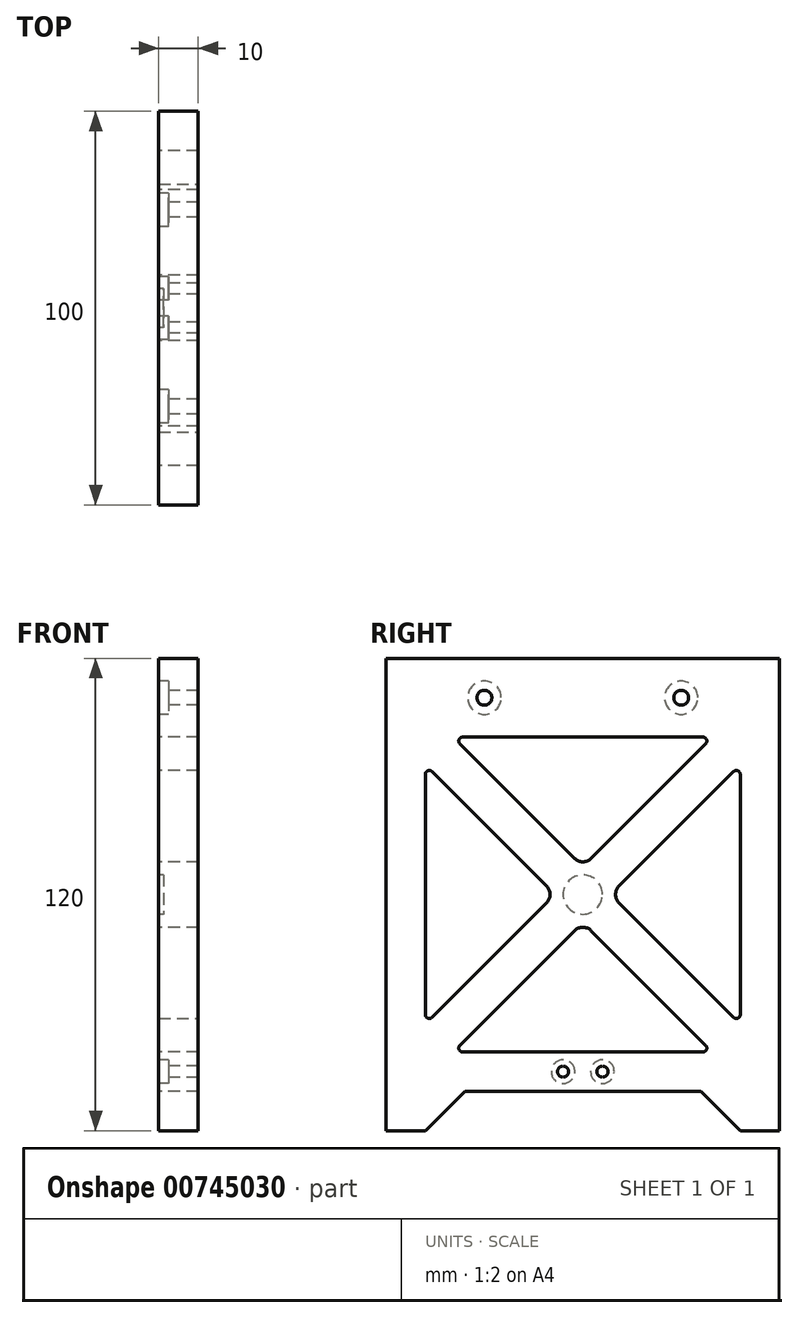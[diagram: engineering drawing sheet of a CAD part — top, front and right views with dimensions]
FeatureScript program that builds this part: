
annotation { "Feature Type Name" : "Feature", "Feature Type Description" : "" }
export const myFeature = defineFeature(function(context is Context, id is Id, definition is map)
    precondition{}
    {
        {
            var Q0;
            Q0=qCreatedBy(makeId("Right.planeOp"),FACE);
            var sketch = newSketch(context, id + "F0", { "sketchPlane" : qUnion([Q0])});
            skLineSegment(sketch, "E0.bottom", {"start": v(50, -60) * mm, "end": v(40.05, -60) * mm});
            skLineSegment(sketch, "E0.top", {"start": v(50, 60) * mm, "end": v(-50, 60) * mm});
            skLineSegment(sketch, "E0.left", {"start": v(50, -60) * mm, "end": v(50, 60) * mm});
            skLineSegment(sketch, "E0.right", {"start": v(-50, -60) * mm, "end": v(-50, 60) * mm});
            skPoint(sketch, "E0.middle", {"position": v(0, 0) * mm});
            skLineSegment(sketch, "E1.bottom", {"start": v(40, -40) * mm, "end": v(-32.93, -40) * mm});
            skLineSegment(sketch, "E1.top", {"start": v(32.93, 40) * mm, "end": v(-32.93, 40) * mm});
            skLineSegment(sketch, "E1.left", {"start": v(40, -40) * mm, "end": v(40, 32.93) * mm});
            skLineSegment(sketch, "E1.right", {"start": v(-40, -32.93) * mm, "end": v(-40, 32.93) * mm});
            skLineSegment(sketch, "E2.trimOffspring", {"start": v(-40, -60) * mm, "end": v(-50, -60) * mm});
            skLineSegment(sketch, "E3", {"start": v(30.05, -50) * mm, "end": v(40.05, -60) * mm});
            skLineSegment(sketch, "E4", {"start": v(30.05, -50) * mm, "end": v(-29.95, -50) * mm});
            skLineSegment(sketch, "E5", {"start": v(-29.95, -50) * mm, "end": v(-40, -60) * mm});
            skLineSegment(sketch, "E6", {"start": v(-40, -32.93) * mm, "end": v(-9.2, -2.12) * mm});
            skLineSegment(sketch, "E7.MirrorCS", {"start": v(-32.93, -40) * mm, "end": v(-2.12, -9.2) * mm});
            skLineSegment(sketch, "E8.trimOffspring", {"start": v(-40, 32.93) * mm, "end": v(-9.2, 2.12) * mm});
            skLineSegment(sketch, "E9.MirrorCS", {"start": v(-32.93, 40) * mm, "end": v(-2.12, 9.2) * mm});
            skLineSegment(sketch, "E10.trimOffspring", {"start": v(9.2, 2.12) * mm, "end": v(40, 32.93) * mm});
            skLineSegment(sketch, "E11.trimOffspring", {"start": v(2.12, -9.2) * mm, "end": v(32.93, -40) * mm});
            skLineSegment(sketch, "E12.trimOffspring", {"start": v(9.2, -2.12) * mm, "end": v(40, -32.93) * mm});
            skLineSegment(sketch, "E13.trimOffspring", {"start": v(2.12, 9.2) * mm, "end": v(32.93, 40) * mm});
            skPoint(sketch, "E14.visualSharp", {"position": v(0, 7.07) * mm});
            skArc(sketch, "E14.filletArc", {"start": v(-2.12, 9.2) * mm, "mid": v(0, 8.31) * mm, "end": v(2.12, 9.2) * mm});
            skPoint(sketch, "E15.visualSharp", {"position": v(0, -7.07) * mm});
            skArc(sketch, "E15.filletArc", {"start": v(2.12, -9.2) * mm, "mid": v(0, -8.31) * mm, "end": v(-2.12, -9.2) * mm});
            skPoint(sketch, "E16.visualSharp", {"position": v(7.07, 0) * mm});
            skArc(sketch, "E16.filletArc", {"start": v(9.2, 2.12) * mm, "mid": v(8.31, 0) * mm, "end": v(9.2, -2.12) * mm});
            skPoint(sketch, "E17.visualSharp", {"position": v(-7.07, 0) * mm});
            skArc(sketch, "E17.filletArc", {"start": v(-9.2, -2.12) * mm, "mid": v(-8.31, 0) * mm, "end": v(-9.2, 2.12) * mm});
            skLineSegment(sketch, "E18", {"start": v(81.83, 50) * mm, "end": v(-92.03, 50) * mm, "construction": true});
            skPoint(sketch, "E19", {"position": v(25, 50) * mm});
            skPoint(sketch, "E20", {"position": v(-25, 50) * mm});
            skSolve(sketch);
        }
        {
            var Q0;
            Q0 = qSketchRegion(id + "F0", true);
            extrude(context, id + "F1", {"entities" : qUnion([Q0]), "depth" : 10 * mm, "offsetDistance" : 25 * mm});
        }
        {
            var Q0;
            Q0=makeQuery(id+"F1.opExtrude","SWEPT_EDGE",EDGE,{"disambiguationData":[OSD([sQuery(id+"F0.wireOp",EDGE,"E1.top"),sQuery(id+"F0.wireOp",EDGE,"E9.MirrorCS")])]});
            var Q1;
            Q1=makeQuery(id+"F1.opExtrude","SWEPT_EDGE",EDGE,{"disambiguationData":[OSD([sQuery(id+"F0.wireOp",EDGE,"E1.top"),sQuery(id+"F0.wireOp",EDGE,"E13.trimOffspring")])]});
            var Q2;
            Q2=makeQuery(id+"F1.opExtrude","SWEPT_EDGE",EDGE,{"disambiguationData":[OSD([sQuery(id+"F0.wireOp",EDGE,"E1.right"),sQuery(id+"F0.wireOp",EDGE,"E8.trimOffspring")])]});
            var Q3;
            Q3=makeQuery(id+"F1.opExtrude","SWEPT_EDGE",EDGE,{"disambiguationData":[OSD([sQuery(id+"F0.wireOp",EDGE,"E1.right"),sQuery(id+"F0.wireOp",EDGE,"E6")])]});
            var Q4;
            Q4=makeQuery(id+"F1.opExtrude","SWEPT_EDGE",EDGE,{"disambiguationData":[OSD([sQuery(id+"F0.wireOp",EDGE,"E1.bottom"),sQuery(id+"F0.wireOp",EDGE,"E7.MirrorCS")])]});
            var Q5;
            Q5=makeQuery(id+"F1.opExtrude","SWEPT_EDGE",EDGE,{"disambiguationData":[OSD([sQuery(id+"F0.wireOp",EDGE,"E1.left"),sQuery(id+"F0.wireOp",EDGE,"E10.trimOffspring")])]});
            var Q6;
            Q6=makeQuery(id+"F1.opExtrude","SWEPT_EDGE",EDGE,{"disambiguationData":[OSD([sQuery(id+"F0.wireOp",EDGE,"E1.left"),sQuery(id+"F0.wireOp",EDGE,"E12.trimOffspring")])]});
            var Q7;
            Q7=makeQuery(id+"F1.opExtrude","SWEPT_EDGE",EDGE,{"disambiguationData":[OSD([sQuery(id+"F0.wireOp",EDGE,"E1.bottom"),sQuery(id+"F0.wireOp",EDGE,"E11.trimOffspring")])]});
            fillet(context, id + "F2", {"entities" : qUnion([Q0, Q1, Q2, Q3, Q4, Q5, Q6, Q7]), "radius" : 1 * mm, "tangentPropagation" : true, "allowEdgeOverflow" : false});
        }
        {
            var Q0;
            Q0=sQuery(id+"F0.wireOp",VERTEX,"E20");
            var Q1;
            Q1=sQuery(id+"F0.wireOp",VERTEX,"E19");
            var Q2;
            Q2=makeQuery(id+"F1.opExtrude","SWEPT_BODY",BODY,{"disambiguationData":[OSD([sQuery(id+"F0.wireOp",EDGE,"E0.bottom"),sQuery(id+"F0.wireOp",EDGE,"E0.top"),sQuery(id+"F0.wireOp",EDGE,"E0.left"),sQuery(id+"F0.wireOp",EDGE,"E0.right"),sQuery(id+"F0.wireOp",EDGE,"E1.bottom"),sQuery(id+"F0.wireOp",EDGE,"E1.top"),sQuery(id+"F0.wireOp",EDGE,"E1.left"),sQuery(id+"F0.wireOp",EDGE,"E1.right"),sQuery(id+"F0.wireOp",EDGE,"E2.trimOffspring"),sQuery(id+"F0.wireOp",EDGE,"E3"),sQuery(id+"F0.wireOp",EDGE,"E4"),sQuery(id+"F0.wireOp",EDGE,"E5"),sQuery(id+"F0.wireOp",EDGE,"E6"),sQuery(id+"F0.wireOp",EDGE,"E7.MirrorCS"),sQuery(id+"F0.wireOp",EDGE,"E8.trimOffspring"),sQuery(id+"F0.wireOp",EDGE,"E9.MirrorCS"),sQuery(id+"F0.wireOp",EDGE,"E10.trimOffspring"),sQuery(id+"F0.wireOp",EDGE,"E11.trimOffspring"),sQuery(id+"F0.wireOp",EDGE,"E12.trimOffspring"),sQuery(id+"F0.wireOp",EDGE,"E13.trimOffspring"),sQuery(id+"F0.wireOp",EDGE,"E14.filletArc"),sQuery(id+"F0.wireOp",EDGE,"E15.filletArc"),sQuery(id+"F0.wireOp",EDGE,"E16.filletArc"),sQuery(id+"F0.wireOp",EDGE,"E17.filletArc")])]});
            hole(context, id + "F3", {"style" : HoleStyle.C_BORE, "endStyle" : HoleEndStyle.THROUGH, "oppositeDirection" : true, "holeDiameter" : 3.8 * mm, "cBoreDiameter" : 8.5 * mm, "cBoreDepth" : 2.5 * mm, "majorDiameter" : 5 * mm, "isTappedThrough" : true, "tappedDepth" : 6 * mm, "tapClearance" : 3, "locations" : qUnion([Q0, Q1]), "scope" : qUnion([Q2])});
        }
        {
            var Q0;
            Q0=makeQuery(id+"F1.opExtrude","CAP_FACE",FACE,{"disambiguationData":[OSD([sQuery(id+"F0.wireOp",EDGE,"E0.bottom"),sQuery(id+"F0.wireOp",EDGE,"E0.top"),sQuery(id+"F0.wireOp",EDGE,"E0.left"),sQuery(id+"F0.wireOp",EDGE,"E0.right"),sQuery(id+"F0.wireOp",EDGE,"E1.bottom"),sQuery(id+"F0.wireOp",EDGE,"E1.top"),sQuery(id+"F0.wireOp",EDGE,"E1.left"),sQuery(id+"F0.wireOp",EDGE,"E1.right"),sQuery(id+"F0.wireOp",EDGE,"E2.trimOffspring"),sQuery(id+"F0.wireOp",EDGE,"E3"),sQuery(id+"F0.wireOp",EDGE,"E4"),sQuery(id+"F0.wireOp",EDGE,"E5"),sQuery(id+"F0.wireOp",EDGE,"E6"),sQuery(id+"F0.wireOp",EDGE,"E7.MirrorCS"),sQuery(id+"F0.wireOp",EDGE,"E8.trimOffspring"),sQuery(id+"F0.wireOp",EDGE,"E9.MirrorCS"),sQuery(id+"F0.wireOp",EDGE,"E10.trimOffspring"),sQuery(id+"F0.wireOp",EDGE,"E11.trimOffspring"),sQuery(id+"F0.wireOp",EDGE,"E12.trimOffspring"),sQuery(id+"F0.wireOp",EDGE,"E13.trimOffspring"),sQuery(id+"F0.wireOp",EDGE,"E14.filletArc"),sQuery(id+"F0.wireOp",EDGE,"E15.filletArc"),sQuery(id+"F0.wireOp",EDGE,"E16.filletArc"),sQuery(id+"F0.wireOp",EDGE,"E17.filletArc")])],"isStart":true});
            var sketch = newSketch(context, id + "F4", { "sketchPlane" : qUnion([Q0])});
            skCircle(sketch, "E21", {"center": v(0, 0) * mm, "radius": 5 * mm});
            skSolve(sketch);
        }
        {
            var Q0;
            Q0=makeQuery(id+"F4.imprint","IMPRINT",FACE,{"disambiguationData":[TD([[makeQuery(id+"F4.imprint","IMPRINT",EDGE,{"derivedFrom":sQuery(id+"F4.wireOp",EDGE,"E21")}),1.0]])]});
            extrude(context, id + "F5", {"entities" : qUnion([Q0]), "operationType" : NewBodyOperationType.REMOVE, "oppositeDirection" : true, "depth" : 1.2 * mm, "offsetDistance" : 25 * mm});
        }
        {
            var Q0;
            Q0=makeQuery(id+"F1.opExtrude","CAP_FACE",FACE,{"disambiguationData":[OSD([sQuery(id+"F0.wireOp",EDGE,"E0.bottom"),sQuery(id+"F0.wireOp",EDGE,"E0.top"),sQuery(id+"F0.wireOp",EDGE,"E0.left"),sQuery(id+"F0.wireOp",EDGE,"E0.right"),sQuery(id+"F0.wireOp",EDGE,"E1.bottom"),sQuery(id+"F0.wireOp",EDGE,"E1.top"),sQuery(id+"F0.wireOp",EDGE,"E1.left"),sQuery(id+"F0.wireOp",EDGE,"E1.right"),sQuery(id+"F0.wireOp",EDGE,"E2.trimOffspring"),sQuery(id+"F0.wireOp",EDGE,"E3"),sQuery(id+"F0.wireOp",EDGE,"E4"),sQuery(id+"F0.wireOp",EDGE,"E5"),sQuery(id+"F0.wireOp",EDGE,"E6"),sQuery(id+"F0.wireOp",EDGE,"E7.MirrorCS"),sQuery(id+"F0.wireOp",EDGE,"E8.trimOffspring"),sQuery(id+"F0.wireOp",EDGE,"E9.MirrorCS"),sQuery(id+"F0.wireOp",EDGE,"E10.trimOffspring"),sQuery(id+"F0.wireOp",EDGE,"E11.trimOffspring"),sQuery(id+"F0.wireOp",EDGE,"E12.trimOffspring"),sQuery(id+"F0.wireOp",EDGE,"E13.trimOffspring"),sQuery(id+"F0.wireOp",EDGE,"E14.filletArc"),sQuery(id+"F0.wireOp",EDGE,"E15.filletArc"),sQuery(id+"F0.wireOp",EDGE,"E16.filletArc"),sQuery(id+"F0.wireOp",EDGE,"E17.filletArc")])],"isStart":true});
            var sketch = newSketch(context, id + "F6", { "sketchPlane" : qUnion([Q0])});
            skPoint(sketch, "E22.0", {"position": v(-50, 60) * mm});
            skPoint(sketch, "E22.1", {"position": v(50, 60) * mm});
            skPoint(sketch, "E22.2", {"position": v(-50, -60) * mm});
            skPoint(sketch, "E22.3", {"position": v(50, -60) * mm});
            skArc(sketch, "E23", {"start": v(-40.05, -60) * mm, "mid": v(-57.03, -67.03) * mm, "end": v(-50, -50.05) * mm});
            skArc(sketch, "E24", {"start": v(40, -60) * mm, "mid": v(57.07, -67.07) * mm, "end": v(50, -50) * mm});
            skArc(sketch, "E25", {"start": v(40, 60) * mm, "mid": v(57.07, 67.07) * mm, "end": v(50, 50) * mm});
            skArc(sketch, "E26", {"start": v(-50, 50) * mm, "mid": v(-57.07, 67.07) * mm, "end": v(-40, 60) * mm});
            skSolve(sketch);
        }
        {
            var Q0;
            {var subQ0=sQuery(id+"F0.wireOp",EDGE,"E0.left");var subQ1=sQuery(id+"F0.wireOp",EDGE,"E0.top");var subQ2=sQuery(id+"F0.wireOp",EDGE,"E0.right");var subQ3=sQuery(id+"F0.wireOp",EDGE,"E2.trimOffspring");var subQ4=sQuery(id+"F0.wireOp",EDGE,"E0.bottom");Q0=makeQuery(id+"FwKSpRcwW1PzX61_1.boolean.opBoolean","MERGE",FACE,{"derivedFrom":[makeQuery(id+"F1.opExtrude","CAP_FACE",FACE,{"disambiguationData":[OSD([subQ4,subQ1,subQ0,subQ2,sQuery(id+"F0.wireOp",EDGE,"E1.bottom"),sQuery(id+"F0.wireOp",EDGE,"E1.top"),sQuery(id+"F0.wireOp",EDGE,"E1.left"),sQuery(id+"F0.wireOp",EDGE,"E1.right"),subQ3,sQuery(id+"F0.wireOp",EDGE,"E3"),sQuery(id+"F0.wireOp",EDGE,"E4"),sQuery(id+"F0.wireOp",EDGE,"E5"),sQuery(id+"F0.wireOp",EDGE,"E6"),sQuery(id+"F0.wireOp",EDGE,"E7.MirrorCS"),sQuery(id+"F0.wireOp",EDGE,"E8.trimOffspring"),sQuery(id+"F0.wireOp",EDGE,"E9.MirrorCS"),sQuery(id+"F0.wireOp",EDGE,"E10.trimOffspring"),sQuery(id+"F0.wireOp",EDGE,"E11.trimOffspring"),sQuery(id+"F0.wireOp",EDGE,"E12.trimOffspring"),sQuery(id+"F0.wireOp",EDGE,"E13.trimOffspring"),sQuery(id+"F0.wireOp",EDGE,"E14.filletArc"),sQuery(id+"F0.wireOp",EDGE,"E15.filletArc"),sQuery(id+"F0.wireOp",EDGE,"E16.filletArc"),sQuery(id+"F0.wireOp",EDGE,"E17.filletArc")])],"isStart":true}),makeQuery(id+"FwKSpRcwW1PzX61_1.opExtrude","CAP_FACE",FACE,{"disambiguationData":[OSD([subQ4,subQ0,sQuery(id+"F6.wireOp",EDGE,"E23")])],"isStart":true}),makeQuery(id+"FwKSpRcwW1PzX61_1.opExtrude","CAP_FACE",FACE,{"disambiguationData":[OSD([subQ2,subQ3,sQuery(id+"F6.wireOp",EDGE,"E24")])],"isStart":true}),makeQuery(id+"FwKSpRcwW1PzX61_1.opExtrude","CAP_FACE",FACE,{"disambiguationData":[OSD([subQ1,subQ2,sQuery(id+"F6.wireOp",EDGE,"E25")])],"isStart":true}),makeQuery(id+"FwKSpRcwW1PzX61_1.opExtrude","CAP_FACE",FACE,{"disambiguationData":[OSD([subQ1,subQ0,sQuery(id+"F6.wireOp",EDGE,"E26")])],"isStart":true})]});}
            var sketch = newSketch(context, id + "F7", { "sketchPlane" : qUnion([Q0])});
            skPoint(sketch, "E27", {"position": v(-5, -45) * mm});
            skPoint(sketch, "E28.MirrorP", {"position": v(5, -45) * mm});
            skSolve(sketch);
        }
        {
            var Q0;
            Q0=sQuery(id+"F7.wireOp",VERTEX,"E27");
            var Q1;
            Q1=sQuery(id+"F7.wireOp",VERTEX,"E28.MirrorP");
            var Q2;
            Q2=makeQuery(id+"F1.opExtrude","SWEPT_BODY",BODY,{"disambiguationData":[OSD([sQuery(id+"F0.wireOp",EDGE,"E0.bottom"),sQuery(id+"F0.wireOp",EDGE,"E0.top"),sQuery(id+"F0.wireOp",EDGE,"E0.left"),sQuery(id+"F0.wireOp",EDGE,"E0.right"),sQuery(id+"F0.wireOp",EDGE,"E1.bottom"),sQuery(id+"F0.wireOp",EDGE,"E1.top"),sQuery(id+"F0.wireOp",EDGE,"E1.left"),sQuery(id+"F0.wireOp",EDGE,"E1.right"),sQuery(id+"F0.wireOp",EDGE,"E2.trimOffspring"),sQuery(id+"F0.wireOp",EDGE,"E3"),sQuery(id+"F0.wireOp",EDGE,"E4"),sQuery(id+"F0.wireOp",EDGE,"E5"),sQuery(id+"F0.wireOp",EDGE,"E6"),sQuery(id+"F0.wireOp",EDGE,"E7.MirrorCS"),sQuery(id+"F0.wireOp",EDGE,"E8.trimOffspring"),sQuery(id+"F0.wireOp",EDGE,"E9.MirrorCS"),sQuery(id+"F0.wireOp",EDGE,"E10.trimOffspring"),sQuery(id+"F0.wireOp",EDGE,"E11.trimOffspring"),sQuery(id+"F0.wireOp",EDGE,"E12.trimOffspring"),sQuery(id+"F0.wireOp",EDGE,"E13.trimOffspring"),sQuery(id+"F0.wireOp",EDGE,"E14.filletArc"),sQuery(id+"F0.wireOp",EDGE,"E15.filletArc"),sQuery(id+"F0.wireOp",EDGE,"E16.filletArc"),sQuery(id+"F0.wireOp",EDGE,"E17.filletArc")])]});
            hole(context, id + "F8", {"style" : HoleStyle.C_BORE, "endStyle" : HoleEndStyle.THROUGH, "holeDiameter" : 2.8 * mm, "cBoreDiameter" : 6 * mm, "cBoreDepth" : 2.5 * mm, "majorDiameter" : 5 * mm, "isTappedThrough" : true, "tappedDepth" : 6 * mm, "tapClearance" : 3, "locations" : qUnion([Q0, Q1]), "scope" : qUnion([Q2])});
        }
    });
